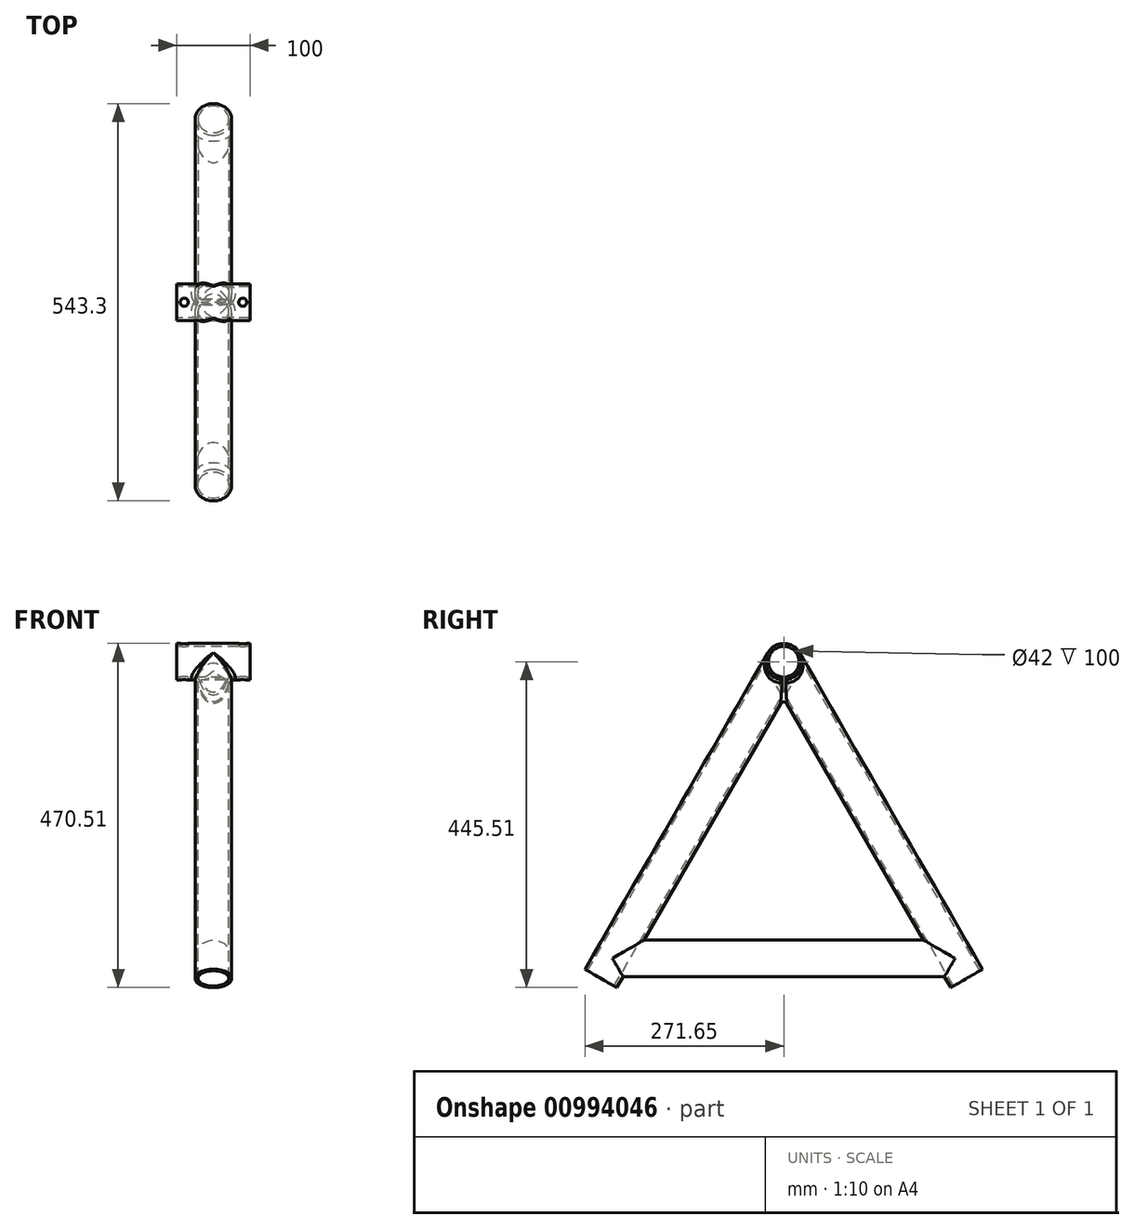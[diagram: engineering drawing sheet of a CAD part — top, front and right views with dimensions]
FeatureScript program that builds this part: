
annotation { "Feature Type Name" : "Feature", "Feature Type Description" : "" }
export const myFeature = defineFeature(function(context is Context, id is Id, definition is map)
    precondition{}
    {
        {
            var Q0;
            Q0=qCreatedBy(makeId("Right.planeOp"),FACE);
            var sketch = newSketch(context, id + "F0", { "sketchPlane" : qUnion([Q0])});
            skCircle(sketch, "E0", {"center": v(0, 0) * mm, "radius": 25 * mm});
            skCircle(sketch, "E1", {"center": v(0, 0) * mm, "radius": 21 * mm});
            skSolve(sketch);
        }
        {
            var Q0;
            Q0=makeQuery(id+"F0.imprint","IMPRINT",FACE,{"disambiguationData":[TD([[makeQuery(id+"F0.imprint","IMPRINT",EDGE,{"derivedFrom":sQuery(id+"F0.wireOp",EDGE,"E0")}),1.0]])]});
            extrude(context, id + "F1", {"entities" : qUnion([Q0]), "endBound" : BoundingType.SYMMETRIC, "depth" : 100 * mm, "offsetDistance" : 25 * mm});
        }
        {
            var Q0;
            Q0=qCreatedBy(makeId("Top.planeOp"),FACE);
            var Q1;
            Q1=makeQuery(id+"F1.opExtrude","SWEPT_FACE",FACE,{"disambiguationData":[OSD([sQuery(id+"F0.wireOp",EDGE,"E0")])]});
            cPlane(context, id + "F2", {"entities" : qUnion([Q0, Q1]), "cplaneType" : CPlaneType.LINE_ANGLE, "offset" : 25 * mm, "angle" : 30 * degree, "width" : 150 * mm, "height" : 150 * mm});
        }
        {
            var Q0;
            Q0=qCreatedBy(id+"F2.planeOp",FACE);
            var sketch = newSketch(context, id + "F3", { "sketchPlane" : qUnion([Q0])});
            skCircle(sketch, "E2", {"center": v(0, 0) * mm, "radius": 25 * mm});
            skCircle(sketch, "E3", {"center": v(0, 0) * mm, "radius": 21 * mm});
            skSolve(sketch);
        }
        {
            var Q0;
            Q0 = qSketchRegion(id + "F3", true);
            var Q1;
            Q1=makeQuery(id+"F1.opExtrude","SWEPT_FACE",FACE,{"disambiguationData":[OSD([sQuery(id+"F0.wireOp",EDGE,"E0")])]});
            extrude(context, id + "F4", {"entities" : qUnion([Q0]), "operationType" : NewBodyOperationType.ADD, "depth" : 500 * mm, "offsetDistance" : 25 * mm, "hasSecondDirection" : true, "secondDirectionBound" : SecondDirectionBoundingType.UP_TO_SURFACE, "secondDirectionOppositeDirection" : false, "secondDirectionDepth" : 25 * mm, "secondDirectionBoundEntityFace" : qUnion([Q1])});
        }
        {
            var Q0;
            Q0=makeQuery(id+"F1.opExtrude","SWEPT_BODY",BODY,{"disambiguationData":[OSD([sQuery(id+"F0.wireOp",EDGE,"E0"),sQuery(id+"F0.wireOp",EDGE,"E1")])]});
            var Q1;
            Q1=qCreatedBy(makeId("Front.planeOp"),FACE);
            mirror(context, id + "F5", {"operationType" : NewBodyOperationType.ADD, "entities" : qUnion([Q0]), "mirrorPlane" : qUnion([Q1])});
        }
        {
            var Q0;
            {var subQ0=makeQuery(id+"F1.opExtrude","SWEPT_FACE",FACE,{"disambiguationData":[OSD([sQuery(id+"F0.wireOp",EDGE,"E0")])]});var subQ1=sQuery(id+"F3.wireOp",EDGE,"E2");var subQ2=makeQuery(id+"F4.opExtrude","SWEPT_FACE",FACE,{"disambiguationData":[OSD([subQ1])]});Q0=makeQuery(id+"F5.boolean.opBoolean","SPLIT",EDGE,{"disambiguationData":[TD([makeQuery(id+"F5.opPattern","COPY",FACE,{"derivedFrom":subQ2,"instanceName":"1"})])],"derivedFrom":makeQuery(id+"F4.opExtrude","CAP_EDGE",EDGE,{"disambiguationData":[OSD([subQ1]),topologyDisambiguationEdgeConnected([subQ0]),OD(1.0)],"isStart":false})});}
            var Q1;
            {var subQ0=makeQuery(id+"F1.opExtrude","SWEPT_FACE",FACE,{"disambiguationData":[OSD([sQuery(id+"F0.wireOp",EDGE,"E0")])]});var subQ1=sQuery(id+"F3.wireOp",EDGE,"E2");var subQ2=makeQuery(id+"F4.opExtrude","SWEPT_FACE",FACE,{"disambiguationData":[OSD([subQ1])]});Q1=makeQuery(id+"F5.boolean.opBoolean","SPLIT",EDGE,{"disambiguationData":[TD([makeQuery(id+"F5.opPattern","COPY",FACE,{"derivedFrom":subQ2,"instanceName":"1"})])],"derivedFrom":makeQuery(id+"F4.opExtrude","CAP_EDGE",EDGE,{"disambiguationData":[OSD([subQ1]),topologyDisambiguationEdgeConnected([subQ0]),OD(0.0)],"isStart":false})});}
            var Q2;
            {var subQ0=makeQuery(id+"F1.opExtrude","SWEPT_FACE",FACE,{"disambiguationData":[OSD([sQuery(id+"F0.wireOp",EDGE,"E0")])]});var subQ1=sQuery(id+"F3.wireOp",EDGE,"E2");var subQ2=makeQuery(id+"F4.opExtrude","SWEPT_FACE",FACE,{"disambiguationData":[OSD([subQ1])]});Q2=makeQuery(id+"F5.boolean.opBoolean","SPLIT",EDGE,{"disambiguationData":[TD([subQ2])],"derivedFrom":makeQuery(id+"F5.opPattern","COPY",EDGE,{"derivedFrom":makeQuery(id+"F4.opExtrude","CAP_EDGE",EDGE,{"disambiguationData":[OSD([subQ1]),topologyDisambiguationEdgeConnected([subQ0]),OD(0.0)],"isStart":false}),"instanceName":"1"})});}
            var Q3;
            {var subQ0=makeQuery(id+"F4.opExtrude","SWEPT_FACE",FACE,{"disambiguationData":[OSD([sQuery(id+"F3.wireOp",EDGE,"E2")])]});Q3=makeQuery(id+"F5.boolean.opBoolean","INTERSECT",EDGE,{"derivedFrom":[subQ0,makeQuery(id+"F5.opPattern","COPY",FACE,{"derivedFrom":subQ0,"instanceName":"1"})]});}
            var Q4;
            {var subQ0=makeQuery(id+"F1.opExtrude","SWEPT_FACE",FACE,{"disambiguationData":[OSD([sQuery(id+"F0.wireOp",EDGE,"E0")])]});var subQ1=sQuery(id+"F3.wireOp",EDGE,"E2");var subQ2=makeQuery(id+"F4.opExtrude","SWEPT_FACE",FACE,{"disambiguationData":[OSD([subQ1])]});Q4=makeQuery(id+"F5.boolean.opBoolean","SPLIT",EDGE,{"disambiguationData":[TD([subQ2])],"derivedFrom":makeQuery(id+"F5.opPattern","COPY",EDGE,{"derivedFrom":makeQuery(id+"F4.opExtrude","CAP_EDGE",EDGE,{"disambiguationData":[OSD([subQ1]),topologyDisambiguationEdgeConnected([subQ0]),OD(1.0)],"isStart":false}),"instanceName":"1"})});}
            fillet(context, id + "F6", {"entities" : qUnion([Q0, Q1, Q2, Q3, Q4]), "radius" : 5 * mm, "tangentPropagation" : true, "allowEdgeOverflow" : false});
        }
        {
            var Q0;
            Q0=qCreatedBy(makeId("Top.planeOp"),FACE);
            var sketch = newSketch(context, id + "F7", { "sketchPlane" : qUnion([Q0])});
            skCircle(sketch, "E4", {"center": v(-40, 0) * mm, "radius": 5.5 * mm});
            skCircle(sketch, "E5", {"center": v(40, 0) * mm, "radius": 5.5 * mm});
            skSolve(sketch);
        }
        {
            var Q0;
            Q0=makeQuery(id+"F7.imprint","IMPRINT",FACE,{"disambiguationData":[TD([[makeQuery(id+"F7.imprint","IMPRINT",EDGE,{"derivedFrom":sQuery(id+"F7.wireOp",EDGE,"E4")}),1.0]])]});
            var Q1;
            Q1=makeQuery(id+"F7.imprint","IMPRINT",FACE,{"disambiguationData":[TD([[makeQuery(id+"F7.imprint","IMPRINT",EDGE,{"derivedFrom":sQuery(id+"F7.wireOp",EDGE,"E5")}),1.0]])]});
            var Q2;
            {var subQ1=sQuery(id+"F0.wireOp",EDGE,"E0");var subQ4=makeQuery(id+"F4.opExtrude","SWEPT_FACE",FACE,{"disambiguationData":[OSD([sQuery(id+"F3.wireOp",EDGE,"E2")])]});Q2=makeQuery(id+"F5.boolean.opBoolean","SPLIT",FACE,{"disambiguationData":[TD([makeQuery(id+"F5.opPattern","COPY",FACE,{"derivedFrom":subQ4,"instanceName":"1"})])],"derivedFrom":makeQuery(id+"F4.boolean.opBoolean","SPLIT",FACE,{"disambiguationData":[TD([subQ4])],"derivedFrom":makeQuery(id+"F1.opExtrude","SWEPT_FACE",FACE,{"disambiguationData":[OSD([subQ1])]})})});}
            var Q3;
            {var subQ1=sQuery(id+"F0.wireOp",EDGE,"E0");var subQ4=makeQuery(id+"F4.opExtrude","SWEPT_FACE",FACE,{"disambiguationData":[OSD([sQuery(id+"F3.wireOp",EDGE,"E2")])]});Q3=makeQuery(id+"F5.boolean.opBoolean","SPLIT",FACE,{"disambiguationData":[TD([makeQuery(id+"F5.opPattern","COPY",FACE,{"derivedFrom":subQ4,"instanceName":"1"})])],"derivedFrom":makeQuery(id+"F4.boolean.opBoolean","SPLIT",FACE,{"disambiguationData":[TD([subQ4])],"derivedFrom":makeQuery(id+"F1.opExtrude","SWEPT_FACE",FACE,{"disambiguationData":[OSD([subQ1])]})})});}
            extrude(context, id + "F8", {"entities" : qUnion([Q0, Q1]), "operationType" : NewBodyOperationType.REMOVE, "endBound" : BoundingType.UP_TO_SURFACE, "depth" : 25 * mm, "endBoundEntityFace" : qUnion([Q2]), "offsetDistance" : 25 * mm, "hasSecondDirection" : true, "secondDirectionBound" : SecondDirectionBoundingType.UP_TO_SURFACE, "secondDirectionOppositeDirection" : true, "secondDirectionDepth" : 25 * mm, "secondDirectionBoundEntityFace" : qUnion([Q3])});
        }
        {
            var Q0;
            Q0=qCreatedBy(makeId("Front.planeOp"),FACE);
            var sketch = newSketch(context, id + "F9", { "sketchPlane" : qUnion([Q0])});
            skLineSegment(sketch, "E6", {"start": v(0, 0) * mm, "end": v(0, -491.17) * mm, "construction": true});
            skCircle(sketch, "E7", {"center": v(0, -405.51) * mm, "radius": 25 * mm});
            skEllipse(sketch, "E8.0", {"center": v(0, -433.01) * mm, "majorRadius": 25 * mm, "minorRadius": 12.5 * mm, "majorAxis": v(-1, 0), "construction": true});
            skPoint(sketch, "E9", {"position": v(0, -445.51) * mm});
            skSolve(sketch);
        }
        {
            var Q0;
            Q0=makeQuery(id+"F9.imprint","IMPRINT",FACE,{"disambiguationData":[TD([[makeQuery(id+"F9.imprint","IMPRINT",EDGE,{"derivedFrom":sQuery(id+"F9.wireOp",EDGE,"E7")}),1.0]])]});
            extrude(context, id + "F10", {"entities" : qUnion([Q0]), "operationType" : NewBodyOperationType.ADD, "endBound" : BoundingType.UP_TO_NEXT, "depth" : 25 * mm, "offsetDistance" : 25 * mm, "hasSecondDirection" : true, "secondDirectionBound" : SecondDirectionBoundingType.UP_TO_NEXT, "secondDirectionOppositeDirection" : true, "secondDirectionDepth" : 25 * mm});
        }
    });
